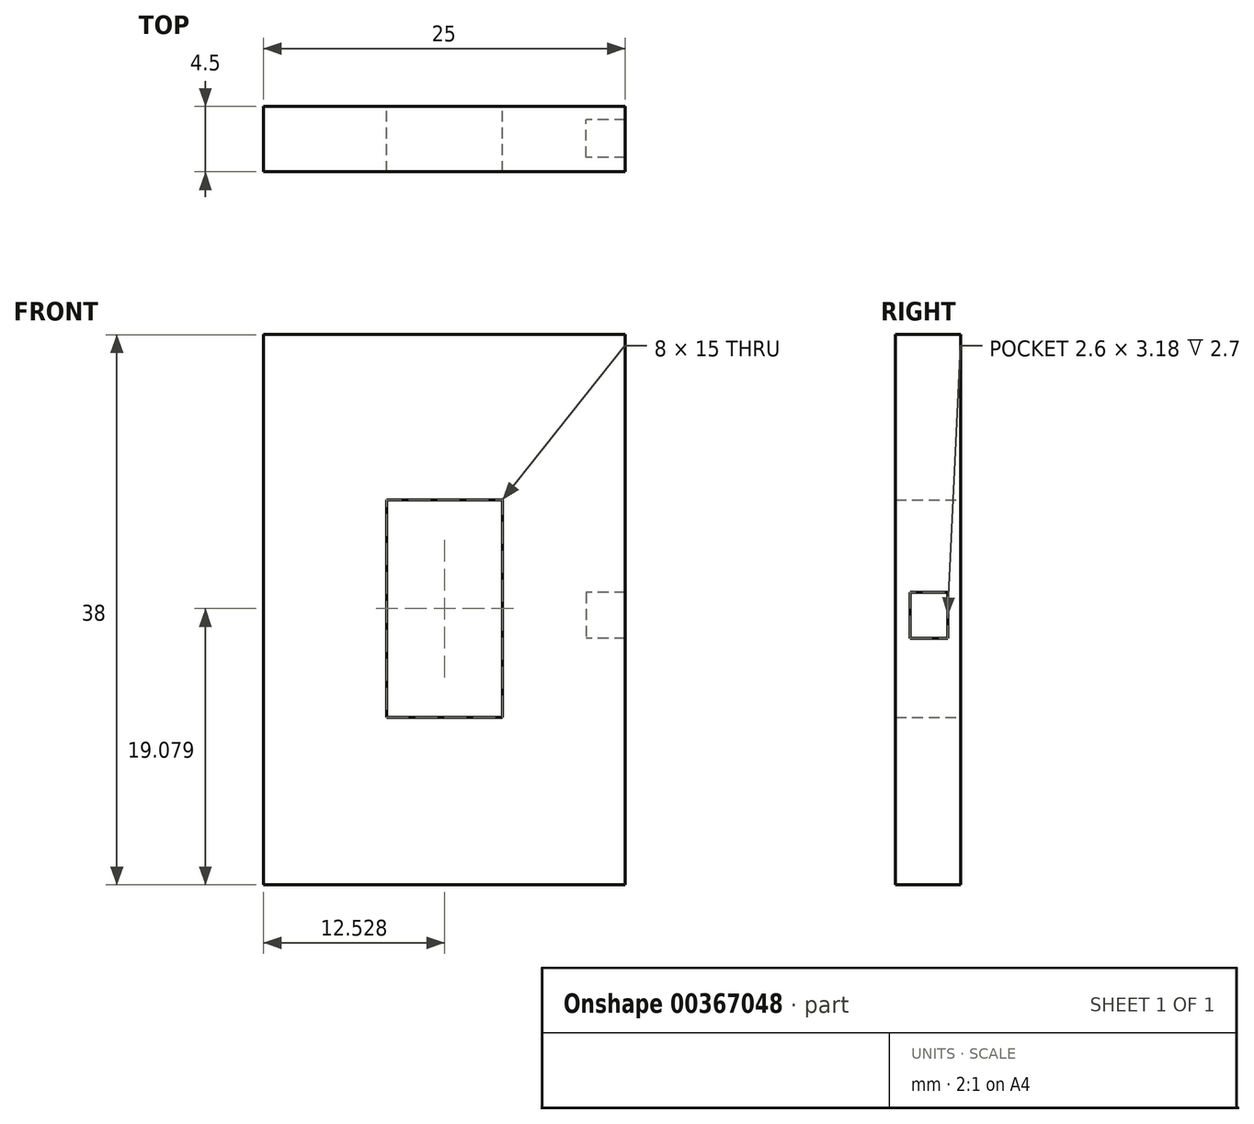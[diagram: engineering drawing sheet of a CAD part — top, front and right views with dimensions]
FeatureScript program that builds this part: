
annotation { "Feature Type Name" : "Feature", "Feature Type Description" : "" }
export const myFeature = defineFeature(function(context is Context, id is Id, definition is map)
    precondition{}
    {
        {
            var Q0;
            Q0=qCreatedBy(makeId("Front.planeOp"),FACE);
            var sketch = newSketch(context, id + "F0", { "sketchPlane" : qUnion([Q0])});
            skLineSegment(sketch, "E0.bottom", {"start": v(-117.14, 21.7) * mm, "end": v(-92.14, 21.7) * mm});
            skLineSegment(sketch, "E0.top", {"start": v(-117.14, -16.3) * mm, "end": v(-92.14, -16.3) * mm});
            skLineSegment(sketch, "E0.left", {"start": v(-117.14, 21.7) * mm, "end": v(-117.14, -16.3) * mm});
            skLineSegment(sketch, "E0.right", {"start": v(-92.14, 21.7) * mm, "end": v(-92.14, 3.89) * mm});
            skLineSegment(sketch, "E1.bottom", {"start": v(-108.61, 10.27) * mm, "end": v(-100.61, 10.27) * mm});
            skLineSegment(sketch, "E1.top", {"start": v(-108.61, -4.73) * mm, "end": v(-100.61, -4.73) * mm});
            skLineSegment(sketch, "E1.left", {"start": v(-108.61, 10.27) * mm, "end": v(-108.61, -4.73) * mm});
            skLineSegment(sketch, "E1.right", {"start": v(-100.61, 10.27) * mm, "end": v(-100.61, -4.73) * mm});
            skLineSegment(sketch, "E2", {"start": v(-92.14, 0.7) * mm, "end": v(-94.84, 0.7) * mm});
            skLineSegment(sketch, "E3", {"start": v(-92.14, 3.89) * mm, "end": v(-94.84, 3.89) * mm});
            skLineSegment(sketch, "E4", {"start": v(-94.84, 0.7) * mm, "end": v(-94.84, 3.89) * mm});
            skLineSegment(sketch, "E5.trimOffspring", {"start": v(-92.14, 0.7) * mm, "end": v(-92.14, -16.3) * mm});
            skSolve(sketch);
        }
        {
            var Q0;
            Q0=makeQuery(id+"F0.imprint","IMPRINT",FACE,{"disambiguationData":[TD([[makeQuery(id+"F0.imprint","IMPRINT",EDGE,{"derivedFrom":sQuery(id+"F0.wireOp",EDGE,"E0.bottom")}),-1.0]])]});
            var Q1;
            Q1 = qSketchRegion(id + "F2", true);
            extrude(context, id + "F1", {"entities" : qUnion([Q0, Q1]), "depth" : 4.5 * mm});
        }
        {
            var Q0;
            Q0=makeQuery(id+"F1.opExtrude","SWEPT_FACE",FACE,{"disambiguationData":[OSD([sQuery(id+"F0.wireOp",EDGE,"E4")])]});
            var sketch = newSketch(context, id + "F2", { "sketchPlane" : qUnion([Q0])});
            skLineSegment(sketch, "E6", {"start": v(-3.5, 3.89) * mm, "end": v(-3.5, 0.7) * mm});
            skLineSegment(sketch, "E7", {"start": v(-0.9, 3.89) * mm, "end": v(-0.9, 0.7) * mm});
            skSolve(sketch);
        }
        {
            var Q0;
            {var subQ0=sQuery(id+"F2.wireOp",EDGE,"E7");Q0=makeQuery(id+"F2.imprint","IMPRINT",FACE,{"disambiguationData":[TD([[makeQuery(id+"F2.imprint","IMPRINT",EDGE,{"derivedFrom":subQ0}),1.0]])]});}
            var Q1;
            {var subQ0=sQuery(id+"F2.wireOp",EDGE,"E6");Q1=makeQuery(id+"F2.imprint","IMPRINT",FACE,{"disambiguationData":[TD([[makeQuery(id+"F2.imprint","IMPRINT",EDGE,{"derivedFrom":subQ0}),-1.0]])]});}
            extrude(context, id + "F3", {"entities" : qUnion([Q0, Q1]), "operationType" : NewBodyOperationType.ADD, "depth" : 2.7 * mm});
        }
    });
